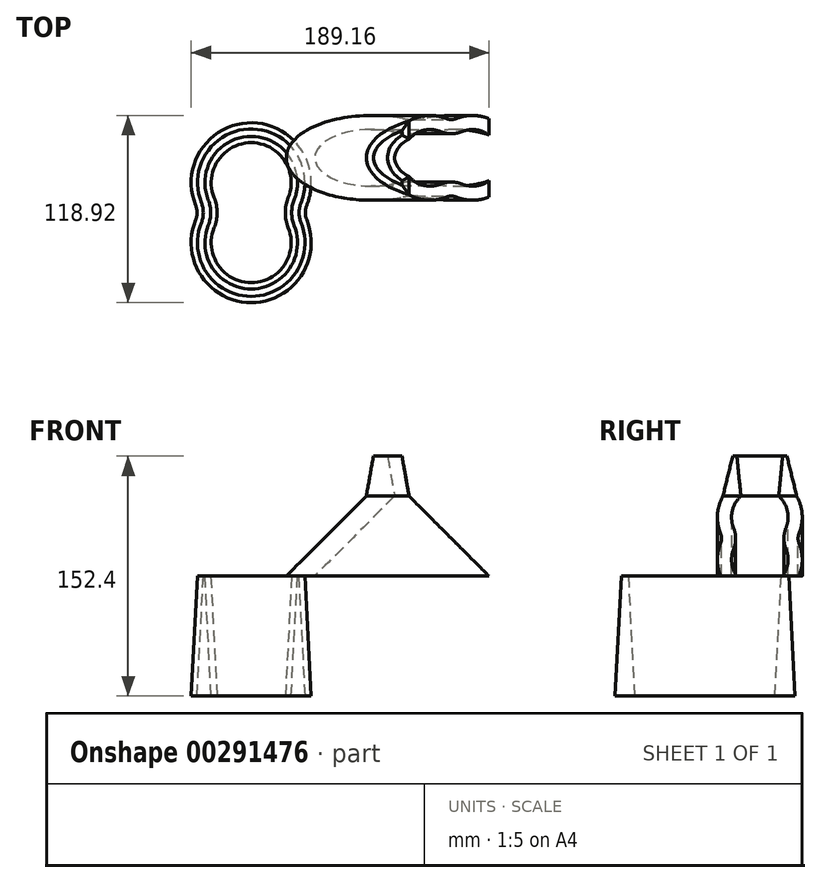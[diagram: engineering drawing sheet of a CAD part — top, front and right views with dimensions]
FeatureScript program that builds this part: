
annotation { "Feature Type Name" : "Feature", "Feature Type Description" : "" }
export const myFeature = defineFeature(function(context is Context, id is Id, definition is map)
    precondition{}
    {
        {
            var Q0;
            Q0=qCreatedBy(makeId("Top.planeOp"),FACE);
            var sketch = newSketch(context, id + "F0", { "sketchPlane" : qUnion([Q0])});
            skArc(sketch, "E0", {"start": v(-35.32, 14.29) * mm, "mid": v(0, -38.1) * mm, "end": v(35.32, 14.29) * mm});
            skArc(sketch, "E1", {"start": v(35.32, 23.81) * mm, "mid": v(0, 76.2) * mm, "end": v(-35.32, 23.81) * mm});
            skPoint(sketch, "E2.visualSharp", {"position": v(33, 19.05) * mm});
            skArc(sketch, "E2.filletArc", {"start": v(35.32, 23.81) * mm, "mid": v(34.4, 19.05) * mm, "end": v(35.32, 14.29) * mm});
            skPoint(sketch, "E3.visualSharp", {"position": v(-33, 19.05) * mm});
            skArc(sketch, "E3.filletArc", {"start": v(-35.32, 14.29) * mm, "mid": v(-34.4, 19.05) * mm, "end": v(-35.32, 23.81) * mm});
            skArc(sketch, "E4.0", {"start": v(23.55, 28.58) * mm, "mid": v(0, 63.5) * mm, "end": v(-23.55, 28.58) * mm});
            skArc(sketch, "E4.1", {"start": v(23.55, 28.58) * mm, "mid": v(21.7, 19.05) * mm, "end": v(23.55, 9.52) * mm});
            skArc(sketch, "E4.2", {"start": v(-23.55, 9.52) * mm, "mid": v(0, -25.4) * mm, "end": v(23.55, 9.52) * mm});
            skArc(sketch, "E4.3", {"start": v(-23.55, 9.52) * mm, "mid": v(-21.7, 19.05) * mm, "end": v(-23.55, 28.58) * mm});
            skSolve(sketch);
        }
        {
            var Q0;
            Q0=makeQuery(id+"F0.imprint","IMPRINT",FACE,{"disambiguationData":[TD([[makeQuery(id+"F0.imprint","IMPRINT",EDGE,{"derivedFrom":sQuery(id+"F0.wireOp",EDGE,"E0")}),1.0]])]});
            extrude(context, id + "F1", {"entities" : qUnion([Q0]), "depth" : 76.2 * mm, "hasDraft" : true, "draftAngle" : 3 * degree, "draftPullDirection" : true});
        }
        {
            var Q0;
            Q0=qCreatedBy(makeId("Top.planeOp"),FACE);
            cPlane(context, id + "F2", {"entities" : qUnion([Q0]), "cplaneType" : CPlaneType.OFFSET, "offset" : 152.4 * mm, "width" : 152.4 * mm, "height" : 152.4 * mm});
        }
        {
            var Q0;
            Q0=qCreatedBy(id+"F2.planeOp",FACE);
            var sketch = newSketch(context, id + "F3", { "sketchPlane" : qUnion([Q0])});
            skLineSegment(sketch, "E5", {"start": v(74.86, 77.26) * mm, "end": v(74.86, -71.47) * mm});
            skSolve(sketch);
        }
        {
            var Q0;
            Q0=sQuery(id+"F3.wireOp",EDGE,"E5");
            cPlane(context, id + "F4", {"entities" : qUnion([Q0]), "cplaneType" : CPlaneType.LINE_ANGLE, "offset" : 25.4 * mm, "angle" : 45 * degree, "oppositeDirection" : true, "width" : 152.4 * mm, "height" : 152.4 * mm});
        }
        {
            var Q0;
            Q0=qCreatedBy(id+"F4.planeOp",FACE);
            var sketch = newSketch(context, id + "F5", { "sketchPlane" : qUnion([Q0])});
            skEllipticalArc(sketch, "E6.0", {});
            skEllipticalArc(sketch, "E7.0.0", {});
            skEllipticalArc(sketch, "E7.0.2", {});
            skEllipticalArc(sketch, "E7.0.3", {});
            skPoint(sketch, "E8.0", {"position": v(-72.04, -19.05) * mm});
            skPoint(sketch, "E9.0", {"position": v(-35.72, -19.05) * mm});
            skEllipticalArc(sketch, "E10.0", {});
            skEllipticalArc(sketch, "E11.0", {});
            const initialGuessF5  = {"E6.0": [-0.05388153672641492, -0.0381, 0, 1, 0.0381, 0.026940768363207464, 1.1863995522992574, 5.0967857548803295], "E7.0.0": [-0.020581855797012598, -0.01905, 0, -1, 0.0127, 0.008980256121069155, 4.327992205889051, 5.096785754880328], "E6.0": [-0.05388153672641492, -0.0381, 0, 1, 0.0381, 0.026940768363207464, 1.1863995522992574, 5.0967857548803295], "E7.0.2": [-0.08718121765581721, -0.01905, 0, -1, 0.0127, 0.008980256121069128, 1.1863995522992565, 1.9551931012905372], "E7.0.3": [-0.05388153672641492, 0, 0, 1, 0.0381, 0.026940768363207464, 4.327992205889051, 1.9551931012905353], "E7.0.0": [-0.020581855797012598, -0.01905, 0, -1, 0.0127, 0.008980256121069155, 4.327992205889051, 5.096785754880328], "E6.0": [-0.05388153672641492, -0.0381, 0, 1, 0.0381, 0.026940768363207464, 1.1863995522992574, 5.0967857548803295], "E7.0.2": [-0.08718121765581721, -0.01905, 0, -1, 0.0127, 0.008980256121069128, 1.1863995522992565, 1.9551931012905372], "E7.0.3": [-0.05388153672641492, 0, 0, 1, 0.0381, 0.026940768363207464, 4.327992205889051, 1.9551931012905353], "E6.0": [-0.05388153672641492, -0.0381, 0, 1, 0.0254, 0.017960512242138307, 1.1863995522992592, 5.096785754880328], "E7.0.0": [-0.020581855797012598, -0.01905, 0, -1, 0.0127, 0.008980256121069155, 4.327992205889051, 5.096785754880328], "E6.0": [-0.05388153672641492, -0.0381, 0, 1, 0.0381, 0.026940768363207464, 1.1863995522992574, 5.0967857548803295], "E7.0.2": [-0.08718121765581721, -0.01905, 0, -1, 0.0127, 0.008980256121069128, 1.1863995522992565, 1.9551931012905372], "E7.0.3": [-0.05388153672641492, 0, 0, 1, 0.0381, 0.026940768363207464, 4.327992205889051, 1.9551931012905353], "E7.0.3": [-0.05388153672641492, 0, 0, 1, 0.0254, 0.017960512242138307, 4.327992205889051, 1.9551931012905353], "E10.0": [-0.020581855797012605, -0.01905, 0, 1, 0.0254, 0.01796051224213831, 1.1863995522992574, 1.9551931012905366], "E11.0": [-0.08718121765581721, -0.01905, 0, 1, 0.0254, 0.01796051224213831, 4.327992205889049, 5.09678575488033]};
            skSetInitialGuess(sketch, initialGuessF5);
            skSolve(sketch);
        }
        {
            var Q0;
            Q0=makeQuery(id+"F5.imprint","IMPRINT",FACE,{"disambiguationData":[TD([[makeQuery(id+"F5.imprint","IMPRINT",EDGE,{"derivedFrom":sQuery(id+"F5.wireOp",EDGE,"E6.0")}),-1.0]])]});
            var Q1;
            Q1=makeQuery(id+"F1.opExtrude","CAP_FACE",FACE,{"disambiguationData":[OSD([sQuery(id+"F0.wireOp",EDGE,"E0"),sQuery(id+"F0.wireOp",EDGE,"E1"),sQuery(id+"F0.wireOp",EDGE,"E2.filletArc"),sQuery(id+"F0.wireOp",EDGE,"E3.filletArc"),sQuery(id+"F0.wireOp",EDGE,"E4.0"),sQuery(id+"F0.wireOp",EDGE,"E4.1"),sQuery(id+"F0.wireOp",EDGE,"E4.2"),sQuery(id+"F0.wireOp",EDGE,"E4.3")])],"isStart":false});
            extrude(context, id + "F6", {"entities" : qUnion([Q0]), "operationType" : NewBodyOperationType.ADD, "endBound" : BoundingType.UP_TO_SURFACE, "endBoundEntityFace" : qUnion([Q1]), "depth" : 101.6 * mm});
        }
        {
            var Q0;
            Q0=qCreatedBy(makeId("Front.planeOp"),FACE);
            var sketch = newSketch(context, id + "F7", { "sketchPlane" : qUnion([Q0])});
            skLineSegment(sketch, "E12.bottom", {"start": v(-29.69, 190.14) * mm, "end": v(124.27, 190.14) * mm});
            skLineSegment(sketch, "E12.top", {"start": v(-29.69, 127) * mm, "end": v(124.27, 127) * mm});
            skLineSegment(sketch, "E12.left", {"start": v(-29.69, 190.14) * mm, "end": v(-29.69, 127) * mm});
            skLineSegment(sketch, "E12.right", {"start": v(124.27, 190.14) * mm, "end": v(124.27, 127) * mm});
            skSolve(sketch);
        }
        {
            var Q0;
            Q0=makeQuery(id+"F7.imprint","IMPRINT",FACE,{"disambiguationData":[TD([[makeQuery(id+"F7.imprint","IMPRINT",EDGE,{"derivedFrom":sQuery(id+"F7.wireOp",EDGE,"E12.bottom")}),-1.0]])]});
            extrude(context, id + "F8", {"entities" : qUnion([Q0]), "operationType" : NewBodyOperationType.REMOVE, "endBound" : BoundingType.SYMMETRIC, "oppositeDirection" : true, "depth" : 177.8 * mm});
        }
        {
            var Q0;
            Q0=makeQuery(id+"F8.boolean.opBoolean","COPY",FACE,{"derivedFrom":makeQuery(id+"F8.opExtrude","SWEPT_FACE",FACE,{"disambiguationData":[OSD([sQuery(id+"F7.wireOp",EDGE,"E12.top")])]})});
            extrude(context, id + "F9", {"entities" : qUnion([Q0]), "operationType" : NewBodyOperationType.ADD, "depth" : 25.4 * mm, "hasDraft" : true, "draftAngle" : 10 * degree, "draftPullDirection" : true});
        }
    });
